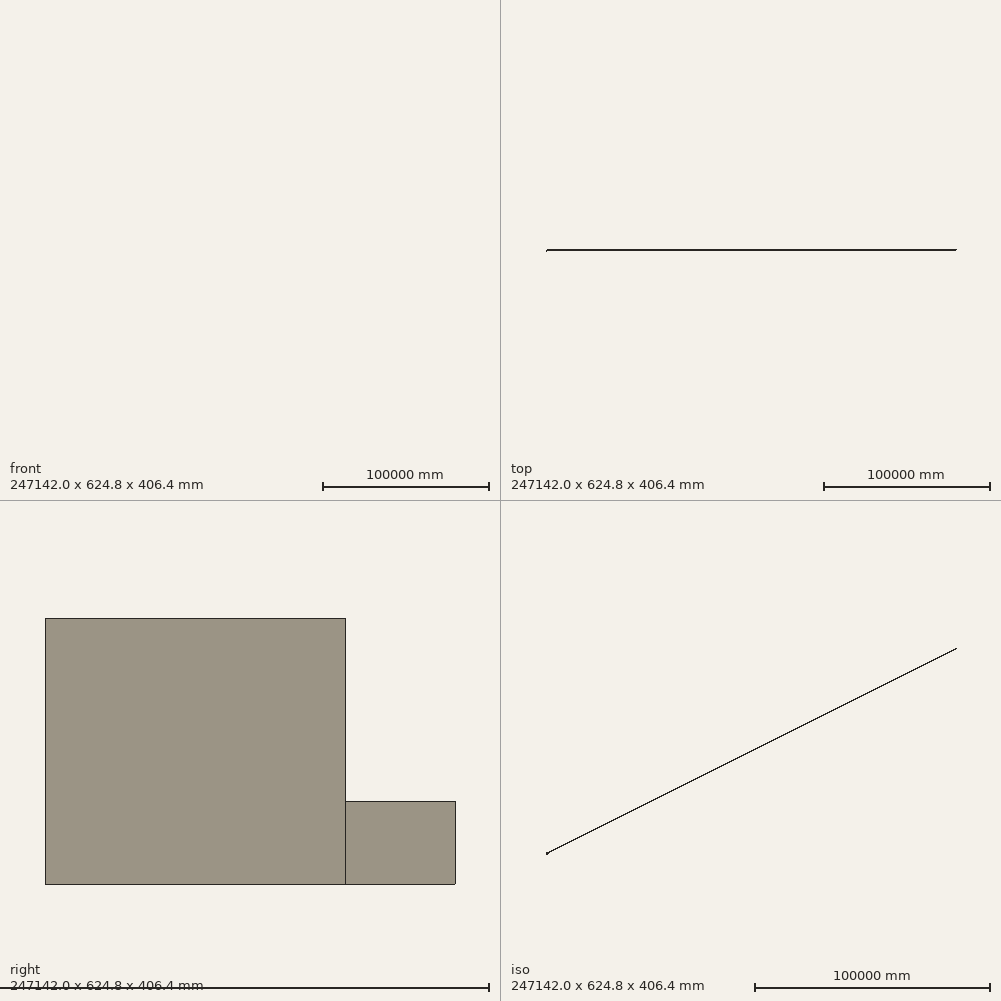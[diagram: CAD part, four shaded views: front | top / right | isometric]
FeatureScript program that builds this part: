
annotation { "Feature Type Name" : "Feature", "Feature Type Description" : "" }
export const myFeature = defineFeature(function(context is Context, id is Id, definition is map)
    precondition{}
    {
        {
            var Q0;
            Q0=qCreatedBy(makeId("Right.planeOp"),FACE);
            var sketch = newSketch(context, id + "F0", { "sketchPlane" : qUnion([Q0])});
            skLineSegment(sketch, "E0.bottom", {"start": v(0, 0) * mm, "end": v(167.64, 0) * mm});
            skLineSegment(sketch, "E0.top", {"start": v(0, 127) * mm, "end": v(167.64, 127) * mm});
            skLineSegment(sketch, "E0.left", {"start": v(0, 0) * mm, "end": v(0, 127) * mm});
            skLineSegment(sketch, "E0.right", {"start": v(167.64, 0) * mm, "end": v(167.64, 127) * mm});
            skSolve(sketch);
        }
        {
            var Q0;
            Q0=makeQuery(id+"F0.imprint","IMPRINT",FACE,{"disambiguationData":[TD([[makeQuery(id+"F0.imprint","IMPRINT",EDGE,{"derivedFrom":sQuery(id+"F0.wireOp",EDGE,"E0.bottom")}),1.0]])]});
            extrude(context, id + "F1", {"entities" : qUnion([Q0]), "depth" : 246583.2 * mm, "offsetDistance" : 25.4 * mm});
        }
        {
            var Q0;
            Q0=qCreatedBy(makeId("Right.planeOp"),FACE);
            var sketch = newSketch(context, id + "F2", { "sketchPlane" : qUnion([Q0])});
            skLineSegment(sketch, "E1.bottom", {"start": v(0, 0) * mm, "end": v(-457.2, 0) * mm});
            skLineSegment(sketch, "E1.top", {"start": v(0, 406.4) * mm, "end": v(-457.2, 406.4) * mm});
            skLineSegment(sketch, "E1.left", {"start": v(0, 0) * mm, "end": v(0, 406.4) * mm});
            skLineSegment(sketch, "E1.right", {"start": v(-457.2, 0) * mm, "end": v(-457.2, 406.4) * mm});
            skSolve(sketch);
        }
        {
            var Q0;
            Q0=makeQuery(id+"F2.imprint","IMPRINT",FACE,{"disambiguationData":[TD([[makeQuery(id+"F2.imprint","IMPRINT",EDGE,{"derivedFrom":sQuery(id+"F2.wireOp",EDGE,"E1.bottom")}),-1.0]])]});
            extrude(context, id + "F3", {"entities" : qUnion([Q0]), "oppositeDirection" : true, "depth" : 558.8 * mm, "offsetDistance" : 25.4 * mm});
        }
    });
